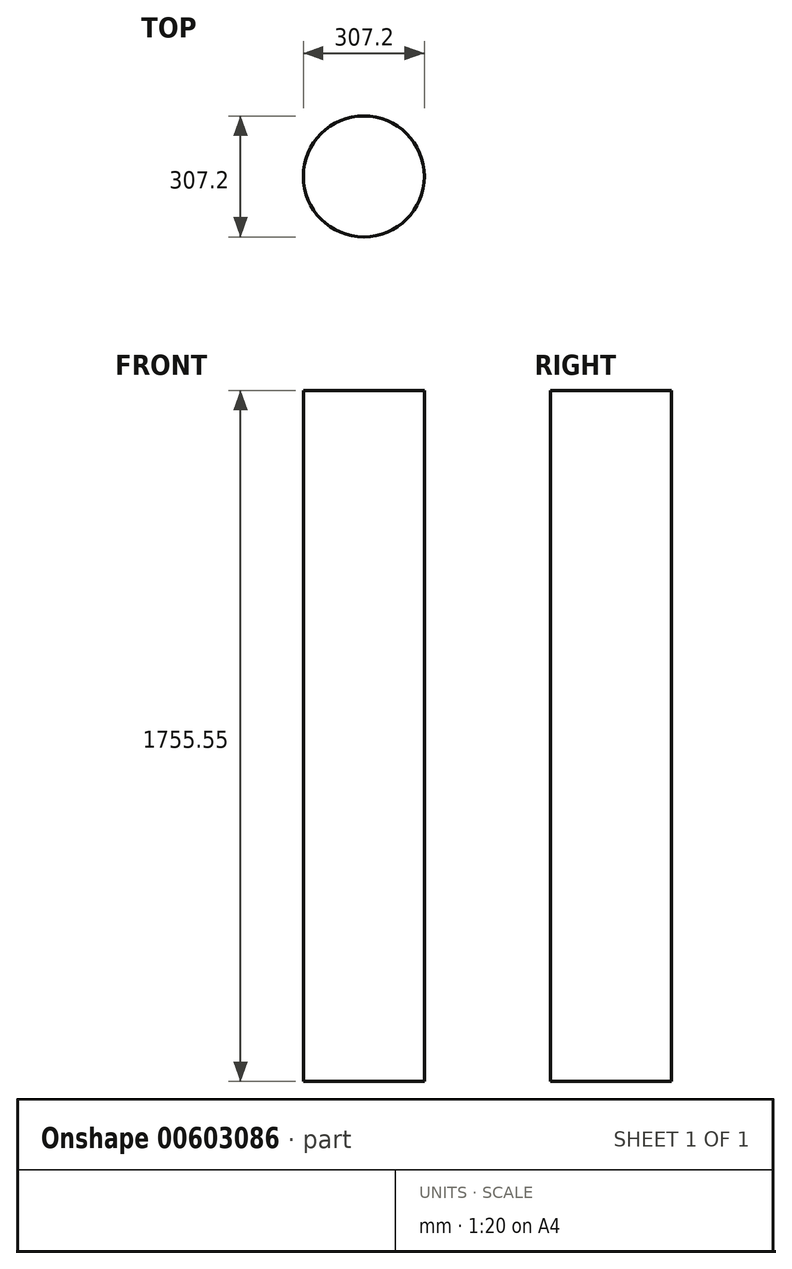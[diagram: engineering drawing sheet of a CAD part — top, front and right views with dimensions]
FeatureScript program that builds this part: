
annotation { "Feature Type Name" : "Feature", "Feature Type Description" : "" }
export const myFeature = defineFeature(function(context is Context, id is Id, definition is map)
    precondition{}
    {
        {
            var Q0;
            Q0=qCreatedBy(makeId("Top.planeOp"),FACE);
            var sketch = newSketch(context, id + "F0", { "sketchPlane" : qUnion([Q0])});
            skCircle(sketch, "E0", {"center": v(0, 0) * mm, "radius": 153.6 * mm});
            skSolve(sketch);
        }
        {
            var Q0;
            Q0=makeQuery(id+"F0.imprint","IMPRINT",FACE,{"disambiguationData":[TD([[makeQuery(id+"F0.imprint","IMPRINT",EDGE,{"derivedFrom":sQuery(id+"F0.wireOp",EDGE,"E0")}),1.0]])]});
            extrude(context, id + "F1", {"entities" : qUnion([Q0]), "depth" : 1755.55 * mm, "offsetDistance" : 25.4 * mm});
        }
    });
